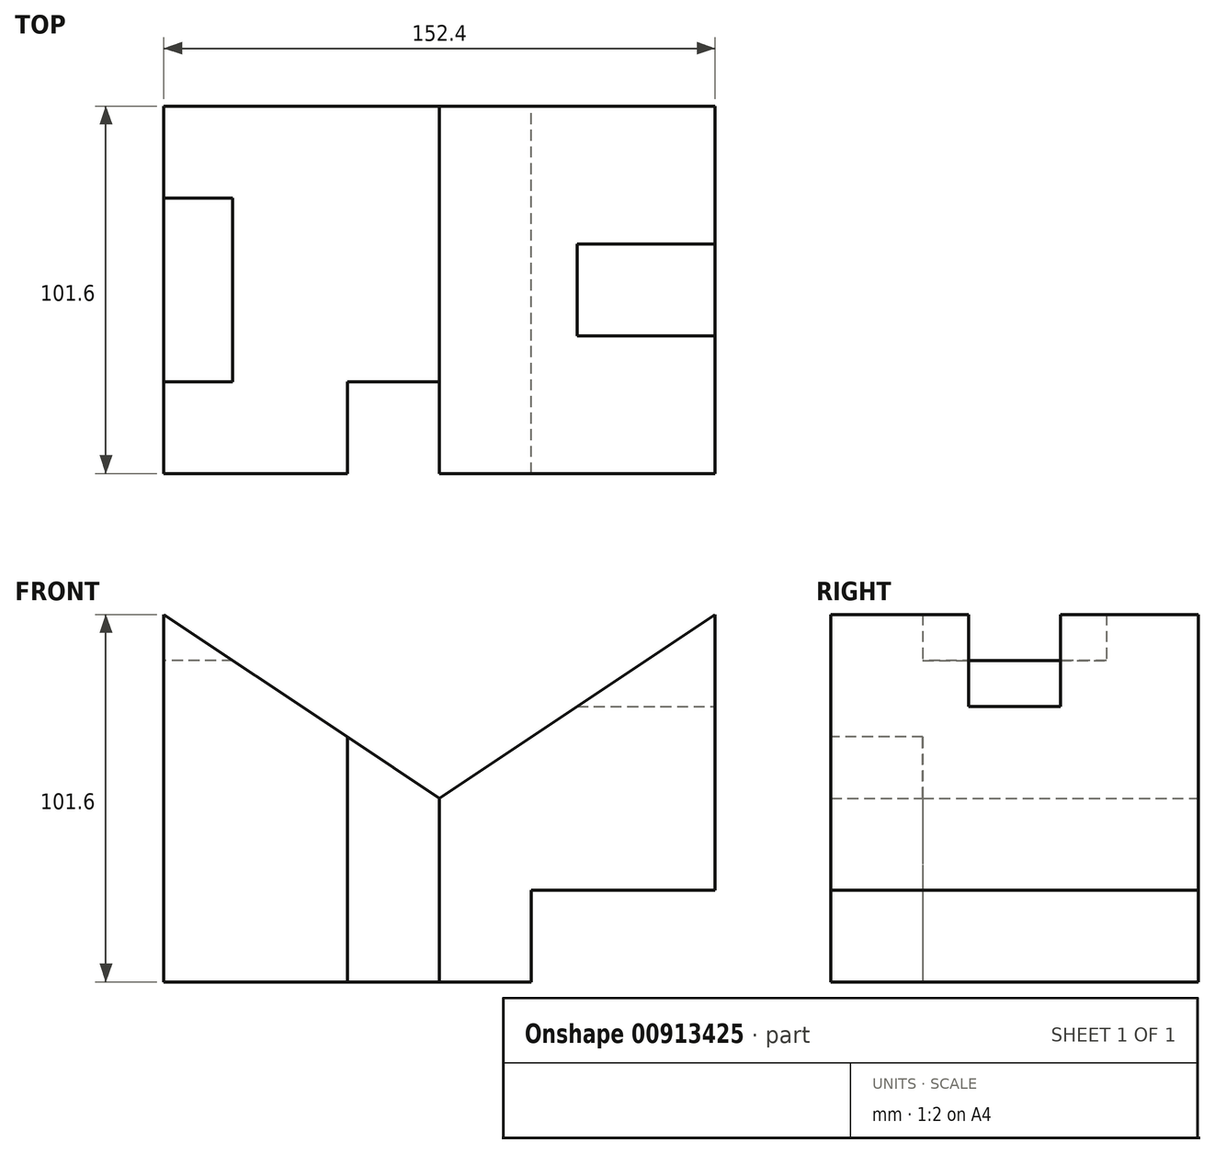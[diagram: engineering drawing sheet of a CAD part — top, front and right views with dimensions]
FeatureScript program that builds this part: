
annotation { "Feature Type Name" : "Feature", "Feature Type Description" : "" }
export const myFeature = defineFeature(function(context is Context, id is Id, definition is map)
    precondition{}
    {
        {
            var Q0;
            Q0=qCreatedBy(makeId("Front.planeOp"),FACE);
            var sketch = newSketch(context, id + "F0", { "sketchPlane" : qUnion([Q0])});
            skLineSegment(sketch, "E0.bottom", {"start": v(0, 0) * mm, "end": v(152.4, 0) * mm});
            skLineSegment(sketch, "E0.top", {"start": v(0, -101.6) * mm, "end": v(152.4, -101.6) * mm});
            skLineSegment(sketch, "E0.left", {"start": v(0, 0) * mm, "end": v(0, -101.6) * mm});
            skLineSegment(sketch, "E0.right", {"start": v(152.4, 0) * mm, "end": v(152.4, -101.6) * mm});
            skLineSegment(sketch, "E1", {"start": v(0, 0) * mm, "end": v(152.4, -101.6) * mm});
            skLineSegment(sketch, "E2", {"start": v(152.4, 0) * mm, "end": v(0, -101.6) * mm});
            skSolve(sketch);
        }
        {
            var Q0;
            {var subQ0=sQuery(id+"F0.wireOp",EDGE,"E0.top");Q0=makeQuery(id+"F0.imprint","IMPRINT",FACE,{"disambiguationData":[TD([[makeQuery(id+"F0.imprint","IMPRINT",EDGE,{"derivedFrom":subQ0}),1.0]])]});}
            var Q1;
            {var subQ0=sQuery(id+"F0.wireOp",EDGE,"E0.left");Q1=makeQuery(id+"F0.imprint","IMPRINT",FACE,{"disambiguationData":[TD([[makeQuery(id+"F0.imprint","IMPRINT",EDGE,{"derivedFrom":subQ0}),1.0]])]});}
            var Q2;
            {var subQ0=sQuery(id+"F0.wireOp",EDGE,"E0.right");Q2=makeQuery(id+"F0.imprint","IMPRINT",FACE,{"disambiguationData":[TD([[makeQuery(id+"F0.imprint","IMPRINT",EDGE,{"derivedFrom":subQ0}),-1.0]])]});}
            extrude(context, id + "F1", {"entities" : qUnion([Q0, Q1, Q2]), "depth" : 101.6 * mm, "offsetDistance" : 25.4 * mm});
        }
        {
            var Q0;
            Q0=makeQuery(id+"F1.opExtrude","SWEPT_FACE",FACE,{"disambiguationData":[OSD([sQuery(id+"F0.wireOp",EDGE,"E0.right")])]});
            var sketch = newSketch(context, id + "F2", { "sketchPlane" : qUnion([Q0])});
            skLineSegment(sketch, "E3.bottom", {"start": v(0, -101.6) * mm, "end": v(-101.6, -101.6) * mm});
            skLineSegment(sketch, "E3.top", {"start": v(0, -76.2) * mm, "end": v(-101.6, -76.2) * mm});
            skLineSegment(sketch, "E3.left", {"start": v(0, -101.6) * mm, "end": v(0, -76.2) * mm});
            skLineSegment(sketch, "E3.right", {"start": v(-101.6, -101.6) * mm, "end": v(-101.6, -76.2) * mm});
            skLineSegment(sketch, "E4.bottom", {"start": v(-63.5, 0) * mm, "end": v(-38.1, 0) * mm});
            skLineSegment(sketch, "E4.top", {"start": v(-63.5, -25.4) * mm, "end": v(-38.1, -25.4) * mm});
            skLineSegment(sketch, "E4.left", {"start": v(-63.5, 0) * mm, "end": v(-63.5, -25.4) * mm});
            skLineSegment(sketch, "E4.right", {"start": v(-38.1, 0) * mm, "end": v(-38.1, -25.4) * mm});
            skSolve(sketch);
        }
        {
            var Q0;
            Q0 = qSketchRegion(id + "F2", true);
            extrude(context, id + "F3", {"entities" : qUnion([Q0]), "operationType" : NewBodyOperationType.REMOVE, "oppositeDirection" : true, "depth" : 50.8 * mm, "offsetDistance" : 25.4 * mm});
        }
        {
            var Q0;
            Q0=makeQuery(id+"F1.opExtrude","SWEPT_FACE",FACE,{"disambiguationData":[OSD([sQuery(id+"F0.wireOp",EDGE,"E0.left")])]});
            var sketch = newSketch(context, id + "F4", { "sketchPlane" : qUnion([Q0])});
            skLineSegment(sketch, "E5.bottom", {"start": v(25.4, 0) * mm, "end": v(76.2, 0) * mm});
            skLineSegment(sketch, "E5.top", {"start": v(25.4, -12.7) * mm, "end": v(76.2, -12.7) * mm});
            skLineSegment(sketch, "E5.left", {"start": v(25.4, 0) * mm, "end": v(25.4, -12.7) * mm});
            skLineSegment(sketch, "E5.right", {"start": v(76.2, 0) * mm, "end": v(76.2, -12.7) * mm});
            skSolve(sketch);
        }
        {
            var Q0;
            Q0 = qSketchRegion(id + "F4", true);
            extrude(context, id + "F5", {"entities" : qUnion([Q0]), "operationType" : NewBodyOperationType.REMOVE, "oppositeDirection" : true, "depth" : 25.4 * mm, "offsetDistance" : 25.4 * mm});
        }
        {
            var Q0;
            Q0=makeQuery(id+"F1.opExtrude","SWEPT_FACE",FACE,{"disambiguationData":[OSD([sQuery(id+"F0.wireOp",EDGE,"E0.top")])]});
            var sketch = newSketch(context, id + "F6", { "sketchPlane" : qUnion([Q0])});
            skLineSegment(sketch, "E6.bottom", {"start": v(50.8, 101.6) * mm, "end": v(76.2, 101.6) * mm});
            skLineSegment(sketch, "E6.top", {"start": v(50.8, 76.2) * mm, "end": v(76.2, 76.2) * mm});
            skLineSegment(sketch, "E6.left", {"start": v(50.8, 101.6) * mm, "end": v(50.8, 76.2) * mm});
            skLineSegment(sketch, "E6.right", {"start": v(76.2, 101.6) * mm, "end": v(76.2, 76.2) * mm});
            skSolve(sketch);
        }
        {
            var Q0;
            Q0 = qSketchRegion(id + "F6", true);
            extrude(context, id + "F7", {"entities" : qUnion([Q0]), "operationType" : NewBodyOperationType.REMOVE, "endBound" : BoundingType.THROUGH_ALL, "oppositeDirection" : true, "depth" : 25.4 * mm, "offsetDistance" : 25.4 * mm});
        }
    });
